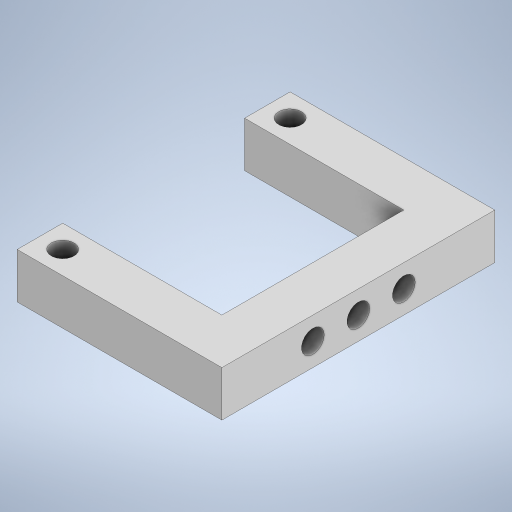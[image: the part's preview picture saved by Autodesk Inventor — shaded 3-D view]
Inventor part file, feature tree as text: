
AUTODESK INVENTOR PART (.ipt)
format: ipt  version: 2023 (Build 270158000, 158)  size: 252,416 bytes
history: native  units: mm
features: extrude x2, sketch x2, other x1
ambient origin geometry x8: Origin, YZ Plane, XZ Plane, XY Plane, X Axis, Y Axis, Z Axis, Center Point
bodies: Body1 (feature_tree)
feature tree (5):
  other  "Твердое тело1"
  extrude  "Выдавливание1"  Depth=90.0mm
  extrude  "Выдавливание2"  Depth=20.0mm
  sketch  "Эскиз1"
  sketch  "Эскиз2"
